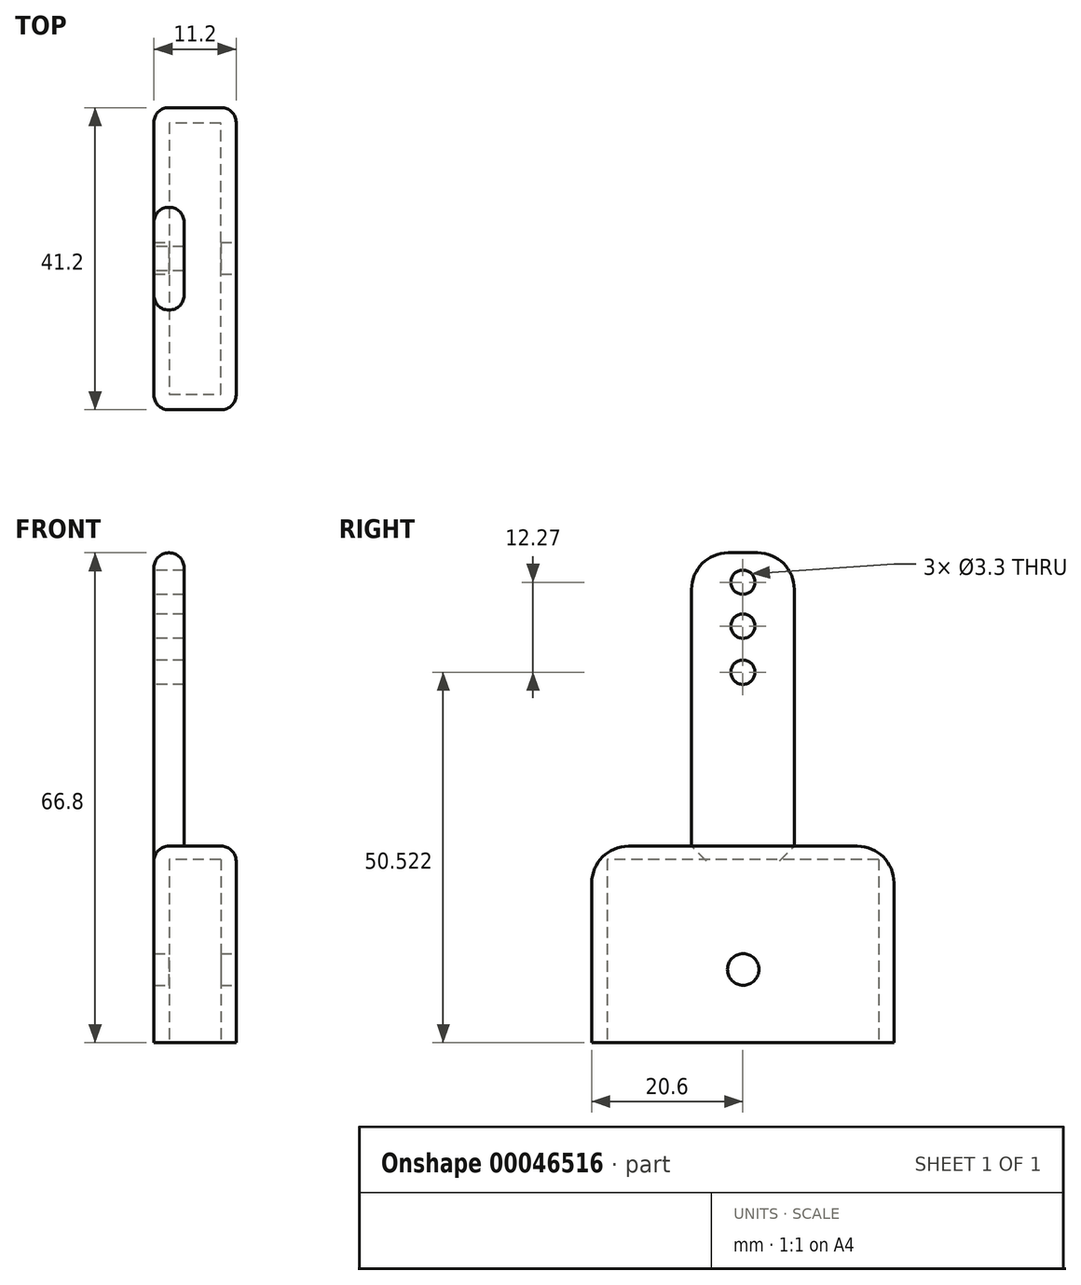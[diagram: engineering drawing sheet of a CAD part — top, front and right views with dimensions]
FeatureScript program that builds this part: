
annotation { "Feature Type Name" : "Feature", "Feature Type Description" : "" }
export const myFeature = defineFeature(function(context is Context, id is Id, definition is map)
    precondition{}
    {
        {
            var Q0;
            Q0=qCreatedBy(makeId("Top.planeOp"),FACE);
            var sketch = newSketch(context, id + "F0", { "sketchPlane" : qUnion([Q0])});
            skLineSegment(sketch, "E0", {"start": v(0, 0) * mm, "end": v(7, 0) * mm});
            skLineSegment(sketch, "E1", {"start": v(7, 0) * mm, "end": v(7, 37) * mm});
            skLineSegment(sketch, "E2", {"start": v(7, 37) * mm, "end": v(0, 37) * mm});
            skLineSegment(sketch, "E3", {"start": v(0, 37) * mm, "end": v(0, 0) * mm});
            skLineSegment(sketch, "E4", {"start": v(0, 18.5) * mm, "end": v(7, 18.5) * mm});
            skLineSegment(sketch, "E5.rect.bottom", {"start": v(-2.1, -2.1) * mm, "end": v(9.1, -2.1) * mm});
            skLineSegment(sketch, "E5.rect.top", {"start": v(-2.1, 39.1) * mm, "end": v(9.1, 39.1) * mm});
            skLineSegment(sketch, "E5.rect.left", {"start": v(-2.1, -2.1) * mm, "end": v(-2.1, 39.1) * mm});
            skLineSegment(sketch, "E5.rect.right", {"start": v(9.1, -2.1) * mm, "end": v(9.1, 39.1) * mm});
            skPoint(sketch, "E5.rect.middle", {"position": v(3.5, 18.5) * mm});
            skSolve(sketch);
        }
        {
            var Q0;
            {var subQ3=sQuery(id+"F0.wireOp",EDGE,"E0");Q0=makeQuery(id+"F0.imprint","IMPRINT",FACE,{"disambiguationData":[TD([[makeQuery(id+"F0.imprint","IMPRINT",EDGE,{"derivedFrom":subQ3}),-1.0]])]});}
            extrude(context, id + "F1", {"entities" : qUnion([Q0]), "depth" : 25 * mm});
        }
        {
            var Q0;
            Q0=qCreatedBy(makeId("Right.planeOp"),FACE);
            var sketch = newSketch(context, id + "F2", { "sketchPlane" : qUnion([Q0])});
            skLineSegment(sketch, "E6", {"start": v(0, 0) * mm, "end": v(-2.1, 0) * mm});
            skLineSegment(sketch, "E7", {"start": v(-2.1, 0) * mm, "end": v(-2.1, 25) * mm});
            skLineSegment(sketch, "E8", {"start": v(-2.1, 25) * mm, "end": v(39.1, 25) * mm});
            skLineSegment(sketch, "E9", {"start": v(-2.1, 25) * mm, "end": v(-2.1, 26.8) * mm});
            skLineSegment(sketch, "E10", {"start": v(18.5, 26.8) * mm, "end": v(25.5, 26.8) * mm});
            skLineSegment(sketch, "E11", {"start": v(39.1, 26.8) * mm, "end": v(39.1, 25) * mm});
            skLineSegment(sketch, "E12", {"start": v(18.5, 26.8) * mm, "end": v(11.5, 26.8) * mm});
            skLineSegment(sketch, "E13", {"start": v(11.5, 26.8) * mm, "end": v(-2.1, 26.8) * mm});
            skLineSegment(sketch, "E14", {"start": v(25.5, 26.8) * mm, "end": v(39.1, 26.8) * mm});
            skLineSegment(sketch, "E15", {"start": v(11.5, 26.8) * mm, "end": v(11.5, 61.8) * mm});
            skLineSegment(sketch, "E16", {"start": v(16.5, 66.8) * mm, "end": v(20.5, 66.8) * mm});
            skLineSegment(sketch, "E17", {"start": v(25.5, 61.8) * mm, "end": v(25.5, 26.8) * mm});
            skCircle(sketch, "E18", {"center": v(18.5, 56.8) * mm, "radius": 1.65 * mm});
            skCircle(sketch, "E19", {"center": v(18.5, 62.8) * mm, "radius": 1.65 * mm});
            skCircle(sketch, "E20", {"center": v(18.5, 50.52) * mm, "radius": 1.65 * mm});
            skPoint(sketch, "E21.start.orphan", {"position": v(18.5, 66.8) * mm});
            skPoint(sketch, "E22.visualSharp", {"position": v(11.5, 66.8) * mm});
            skArc(sketch, "E22.filletArc", {"start": v(16.5, 66.8) * mm, "mid": v(12.96, 65.34) * mm, "end": v(11.5, 61.8) * mm});
            skPoint(sketch, "E23.visualSharp", {"position": v(25.5, 66.8) * mm});
            skArc(sketch, "E23.filletArc", {"start": v(25.5, 61.8) * mm, "mid": v(24.04, 65.34) * mm, "end": v(20.5, 66.8) * mm});
            skSolve(sketch);
        }
        {
            var Q0;
            Q0=makeQuery(id+"F2.imprint","IMPRINT",FACE,{"disambiguationData":[TD([[makeQuery(id+"F2.imprint","IMPRINT",EDGE,{"derivedFrom":sQuery(id+"F2.wireOp",EDGE,"E8")}),1.0]])]});
            extrude(context, id + "F3", {"entities" : qUnion([Q0]), "operationType" : NewBodyOperationType.ADD, "oppositeDirection" : true, "depth" : 2.1 * mm, "hasSecondDirection" : true, "secondDirectionOppositeDirection" : false, "secondDirectionDepth" : 9.1 * mm});
        }
        {
            var Q0;
            Q0=makeQuery(id+"F2.imprint","IMPRINT",FACE,{"disambiguationData":[TD([[makeQuery(id+"F2.imprint","IMPRINT",EDGE,{"derivedFrom":sQuery(id+"F2.wireOp",EDGE,"E10")}),1.0]])]});
            extrude(context, id + "F4", {"entities" : qUnion([Q0]), "operationType" : NewBodyOperationType.ADD, "depth" : 2 * mm, "hasSecondDirection" : true, "secondDirectionOppositeDirection" : true, "secondDirectionDepth" : 2.1 * mm});
        }
        {
            var Q0;
            Q0=makeQuery(id+"F3.opExtrude","SWEPT_EDGE",EDGE,{"disambiguationData":[OSD([sQuery(id+"F2.wireOp",EDGE,"E9"),sQuery(id+"F2.wireOp",EDGE,"E13")])]});
            var Q1;
            Q1=makeQuery(id+"F3.opExtrude","SWEPT_EDGE",EDGE,{"disambiguationData":[OSD([sQuery(id+"F2.wireOp",EDGE,"E11"),sQuery(id+"F2.wireOp",EDGE,"E14")])]});
            fillet(context, id + "F5", {"entities" : qUnion([Q0, Q1]), "radius" : 5 * mm, "tangentPropagation" : true, "allowEdgeOverflow" : false});
        }
        {
            var Q0;
            Q0=makeQuery(id+"F3.boolean.opBoolean","MERGE",EDGE,{"derivedFrom":[makeQuery(id+"F1.opExtrude","SWEPT_EDGE",EDGE,{"disambiguationData":[OSD([sQuery(id+"F0.wireOp",EDGE,"E5.rect.bottom"),sQuery(id+"F0.wireOp",EDGE,"E5.rect.left")])]}),makeQuery(id+"F3.opExtrude","CAP_EDGE",EDGE,{"disambiguationData":[OSD([sQuery(id+"F2.wireOp",EDGE,"E9")])],"isStart":false})]});
            var Q1;
            Q1=makeQuery(id+"F3.boolean.opBoolean","MERGE",EDGE,{"derivedFrom":[makeQuery(id+"F1.opExtrude","SWEPT_EDGE",EDGE,{"disambiguationData":[OSD([sQuery(id+"F0.wireOp",EDGE,"E5.rect.top"),sQuery(id+"F0.wireOp",EDGE,"E5.rect.left")])]}),makeQuery(id+"F3.opExtrude","CAP_EDGE",EDGE,{"disambiguationData":[OSD([sQuery(id+"F2.wireOp",EDGE,"E11")])],"isStart":false})]});
            var Q2;
            Q2=makeQuery(id+"F3.boolean.opBoolean","MERGE",EDGE,{"derivedFrom":[makeQuery(id+"F1.opExtrude","SWEPT_EDGE",EDGE,{"disambiguationData":[OSD([sQuery(id+"F0.wireOp",EDGE,"E5.rect.bottom"),sQuery(id+"F0.wireOp",EDGE,"E5.rect.right")])]}),makeQuery(id+"F3.opExtrude","CAP_EDGE",EDGE,{"disambiguationData":[OSD([sQuery(id+"F2.wireOp",EDGE,"E9")])],"isStart":true})]});
            var Q3;
            Q3=makeQuery(id+"F4.opExtrude","CAP_EDGE",EDGE,{"disambiguationData":[OSD([sQuery(id+"F2.wireOp",EDGE,"E15")])],"isStart":true});
            var Q4;
            Q4=makeQuery(id+"F4.opExtrude","CAP_EDGE",EDGE,{"disambiguationData":[OSD([sQuery(id+"F2.wireOp",EDGE,"E15")])],"isStart":false});
            fillet(context, id + "F6", {"entities" : qUnion([Q0, Q1, Q2, Q3, Q4]), "radius" : 2 * mm, "tangentPropagation" : true, "allowEdgeOverflow" : false});
        }
        {
            var Q0;
            Q0=qCreatedBy(makeId("Right.planeOp"),FACE);
            var sketch = newSketch(context, id + "F7", { "sketchPlane" : qUnion([Q0])});
            skLineSegment(sketch, "E24", {"start": v(0, 0) * mm, "end": v(37.1, 0) * mm});
            skLineSegment(sketch, "E25", {"start": v(18.55, 0) * mm, "end": v(18.55, 10) * mm});
            skCircle(sketch, "E26", {"center": v(18.55, 10) * mm, "radius": 2.15 * mm});
            skSolve(sketch);
        }
        {
            var Q0;
            Q0 = qSketchRegion(id + "F7", true);
            extrude(context, id + "F8", {"entities" : qUnion([Q0]), "operationType" : NewBodyOperationType.REMOVE, "endBound" : BoundingType.THROUGH_ALL, "oppositeDirection" : true, "depth" : 25 * mm, "hasSecondDirection" : true, "secondDirectionBound" : SecondDirectionBoundingType.THROUGH_ALL, "secondDirectionOppositeDirection" : false, "secondDirectionDepth" : 25 * mm});
        }
    });
